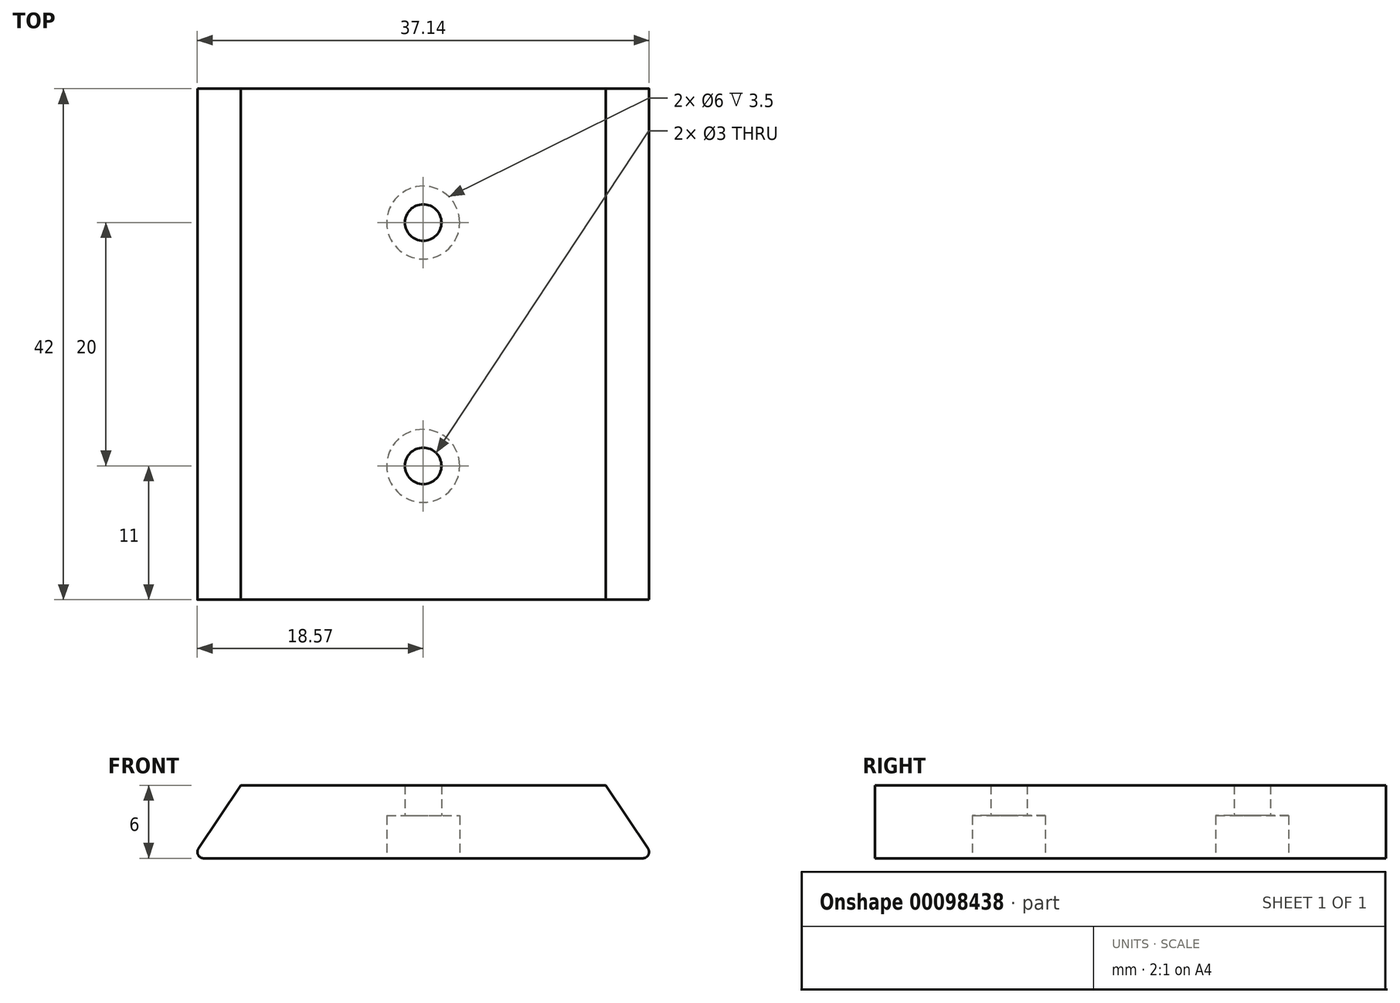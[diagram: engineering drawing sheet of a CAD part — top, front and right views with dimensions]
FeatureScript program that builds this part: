
annotation { "Feature Type Name" : "Feature", "Feature Type Description" : "" }
export const myFeature = defineFeature(function(context is Context, id is Id, definition is map)
    precondition{}
    {
        {
            var Q0;
            Q0=qCreatedBy(makeId("Top.planeOp"),FACE);
            var sketch = newSketch(context, id + "F0", { "sketchPlane" : qUnion([Q0])});
            skLineSegment(sketch, "E0.bottom", {"start": v(19, -21) * mm, "end": v(-19, -21) * mm});
            skLineSegment(sketch, "E0.top", {"start": v(19, 21) * mm, "end": v(-19, 21) * mm});
            skLineSegment(sketch, "E0.left", {"start": v(19, -21) * mm, "end": v(19, 21) * mm});
            skLineSegment(sketch, "E0.right", {"start": v(-19, -21) * mm, "end": v(-19, 21) * mm});
            skPoint(sketch, "E0.middle", {"position": v(0, 0) * mm});
            skSolve(sketch);
        }
        {
            var Q0;
            Q0=makeQuery(id+"F0.imprint","IMPRINT",FACE,{"disambiguationData":[TD([[makeQuery(id+"F0.imprint","IMPRINT",EDGE,{"derivedFrom":sQuery(id+"F0.wireOp",EDGE,"E0.bottom")}),-1.0]])]});
            extrude(context, id + "F1", {"entities" : qUnion([Q0]), "depth" : 6 * mm});
        }
        {
            var Q0;
            Q0=makeQuery(id+"F1.opExtrude","SWEPT_FACE",FACE,{"disambiguationData":[OSD([sQuery(id+"F0.wireOp",EDGE,"E0.bottom")])]});
            var sketch = newSketch(context, id + "F2", { "sketchPlane" : qUnion([Q0])});
            skLineSegment(sketch, "E1", {"start": v(19, 0) * mm, "end": v(15, 6) * mm});
            skLineSegment(sketch, "E2", {"start": v(-19, 6) * mm, "end": v(-15, 6) * mm});
            skLineSegment(sketch, "E3", {"start": v(-19, 0) * mm, "end": v(-15, 6) * mm});
            skLineSegment(sketch, "E4", {"start": v(-19, 6) * mm, "end": v(-19, 0) * mm});
            skLineSegment(sketch, "E5", {"start": v(15, 6) * mm, "end": v(19, 6) * mm});
            skLineSegment(sketch, "E6", {"start": v(19, 6) * mm, "end": v(19, 0) * mm});
            skSolve(sketch);
        }
        {
            var Q0;
            Q0 = qSketchRegion(id + "F2", true);
            extrude(context, id + "F3", {"entities" : qUnion([Q0]), "operationType" : NewBodyOperationType.REMOVE, "oppositeDirection" : true, "depth" : 42 * mm});
        }
        {
            var Q0;
            Q0=makeQuery(id+"F3.boolean.opBoolean","MERGE",EDGE,{"derivedFrom":[makeQuery(id+"F1.opExtrude","CAP_EDGE",EDGE,{"disambiguationData":[OSD([sQuery(id+"F0.wireOp",EDGE,"E0.right")])],"isStart":true}),makeQuery(id+"F3.opExtrude","SWEPT_EDGE",EDGE,{"disambiguationData":[OSD([sQuery(id+"F0.wireOp",EDGE,"E0.bottom"),sQuery(id+"F2.wireOp",EDGE,"E3"),sQuery(id+"F2.wireOp",EDGE,"E4")])]})]});
            var Q1;
            Q1=makeQuery(id+"F3.boolean.opBoolean","MERGE",EDGE,{"derivedFrom":[makeQuery(id+"F1.opExtrude","CAP_EDGE",EDGE,{"disambiguationData":[OSD([sQuery(id+"F0.wireOp",EDGE,"E0.left")])],"isStart":true}),makeQuery(id+"F3.opExtrude","SWEPT_EDGE",EDGE,{"disambiguationData":[OSD([sQuery(id+"F0.wireOp",EDGE,"E0.bottom"),sQuery(id+"F2.wireOp",EDGE,"E1"),sQuery(id+"F2.wireOp",EDGE,"E6")])]})]});
            var Q2;
            Q2=makeQuery(id+"F3.boolean.opBoolean","COPY",EDGE,{"derivedFrom":makeQuery(id+"F3.opExtrude","SWEPT_EDGE",EDGE,{"disambiguationData":[OSD([sQuery(id+"F0.wireOp",EDGE,"E0.bottom"),sQuery(id+"F2.wireOp",EDGE,"E2"),sQuery(id+"F2.wireOp",EDGE,"E3")])]})});
            var Q3;
            Q3=makeQuery(id+"F3.boolean.opBoolean","COPY",EDGE,{"derivedFrom":makeQuery(id+"F3.opExtrude","SWEPT_EDGE",EDGE,{"disambiguationData":[OSD([sQuery(id+"F0.wireOp",EDGE,"E0.bottom"),sQuery(id+"F2.wireOp",EDGE,"E1"),sQuery(id+"F2.wireOp",EDGE,"E5")])]})});
            fillet(context, id + "F4", {"entities" : qUnion([Q0, Q1, Q2, Q3]), "radius" : 0.5 * mm, "tangentPropagation" : true, "allowEdgeOverflow" : false});
        }
        {
            var Q0;
            Q0=makeQuery(id+"F1.opExtrude","CAP_FACE",FACE,{"disambiguationData":[OSD([sQuery(id+"F0.wireOp",EDGE,"E0.bottom"),sQuery(id+"F0.wireOp",EDGE,"E0.top"),sQuery(id+"F0.wireOp",EDGE,"E0.left"),sQuery(id+"F0.wireOp",EDGE,"E0.right")])],"isStart":true});
            var sketch = newSketch(context, id + "F5", { "sketchPlane" : qUnion([Q0])});
            skCircle(sketch, "E7", {"center": v(0, 10) * mm, "radius": 3 * mm});
            skCircle(sketch, "E8", {"center": v(0, -10) * mm, "radius": 3 * mm});
            skSolve(sketch);
        }
        {
            var Q0;
            Q0 = qSketchRegion(id + "F5", true);
            extrude(context, id + "F6", {"entities" : qUnion([Q0]), "operationType" : NewBodyOperationType.REMOVE, "oppositeDirection" : true, "depth" : 3.5 * mm});
        }
        {
            var Q0;
            Q0=makeQuery(id+"F6.boolean.opBoolean","COPY",FACE,{"derivedFrom":makeQuery(id+"F6.opExtrude","CAP_FACE",FACE,{"disambiguationData":[OSD([sQuery(id+"F5.wireOp",EDGE,"E7")])],"isStart":false})});
            var sketch = newSketch(context, id + "F7", { "sketchPlane" : qUnion([Q0])});
            skCircle(sketch, "E9", {"center": v(0, 10) * mm, "radius": 1.5 * mm});
            skSolve(sketch);
        }
        {
            var Q0;
            Q0=makeQuery(id+"F6.boolean.opBoolean","COPY",FACE,{"derivedFrom":makeQuery(id+"F6.opExtrude","CAP_FACE",FACE,{"disambiguationData":[OSD([sQuery(id+"F5.wireOp",EDGE,"E8")])],"isStart":false})});
            var sketch = newSketch(context, id + "F8", { "sketchPlane" : qUnion([Q0])});
            skCircle(sketch, "E10", {"center": v(0, -10) * mm, "radius": 1.5 * mm});
            skSolve(sketch);
        }
        {
            var Q0;
            Q0 = qSketchRegion(id + "F7", true);
            var Q1;
            Q1 = qSketchRegion(id + "F8", true);
            var Q2;
            Q2=sQuery(id+"F7.wireOp",EDGE,"E9");
            extrude(context, id + "F9", {"entities" : qUnion([Q0, Q1]), "operationType" : NewBodyOperationType.REMOVE, "surfaceEntities" : qUnion([Q2]), "oppositeDirection" : true, "depth" : 5 * mm});
        }
    });
